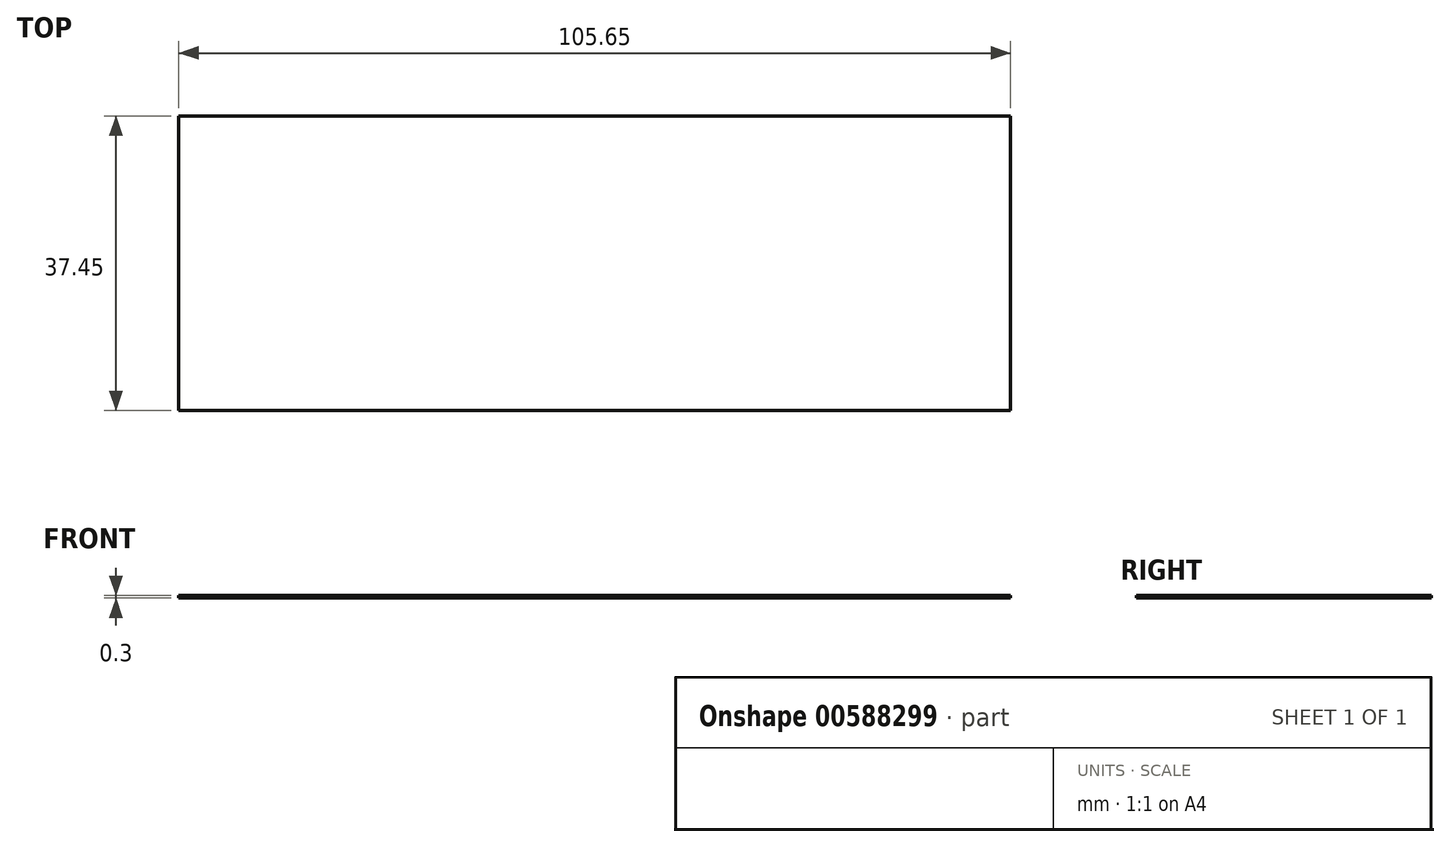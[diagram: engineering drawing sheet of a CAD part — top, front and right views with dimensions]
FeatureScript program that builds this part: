
annotation { "Feature Type Name" : "Feature", "Feature Type Description" : "" }
export const myFeature = defineFeature(function(context is Context, id is Id, definition is map)
    precondition{}
    {
        {
            var Q0;
            Q0=qCreatedBy(makeId("Top.planeOp"),FACE);
            var sketch = newSketch(context, id + "F0", { "sketchPlane" : qUnion([Q0])});
            skLineSegment(sketch, "E0.bottom", {"start": v(-66.7, 11.04) * mm, "end": v(38.95, 11.04) * mm});
            skLineSegment(sketch, "E0.top", {"start": v(-66.7, -26.41) * mm, "end": v(38.95, -26.41) * mm});
            skLineSegment(sketch, "E0.left", {"start": v(-66.7, 11.04) * mm, "end": v(-66.7, -26.41) * mm});
            skLineSegment(sketch, "E0.right", {"start": v(38.95, 11.04) * mm, "end": v(38.95, -26.41) * mm});
            skSolve(sketch);
        }
        {
            var Q0;
            Q0=makeQuery(id+"F0.imprint","IMPRINT",FACE,{"disambiguationData":[TD([[makeQuery(id+"F0.imprint","IMPRINT",EDGE,{"derivedFrom":sQuery(id+"F0.wireOp",EDGE,"E0.bottom")}),-1.0]])]});
            extrude(context, id + "F1", {"entities" : qUnion([Q0]), "depth" : .3 * mm, "offsetDistance" : 25 * mm});
        }
    });
